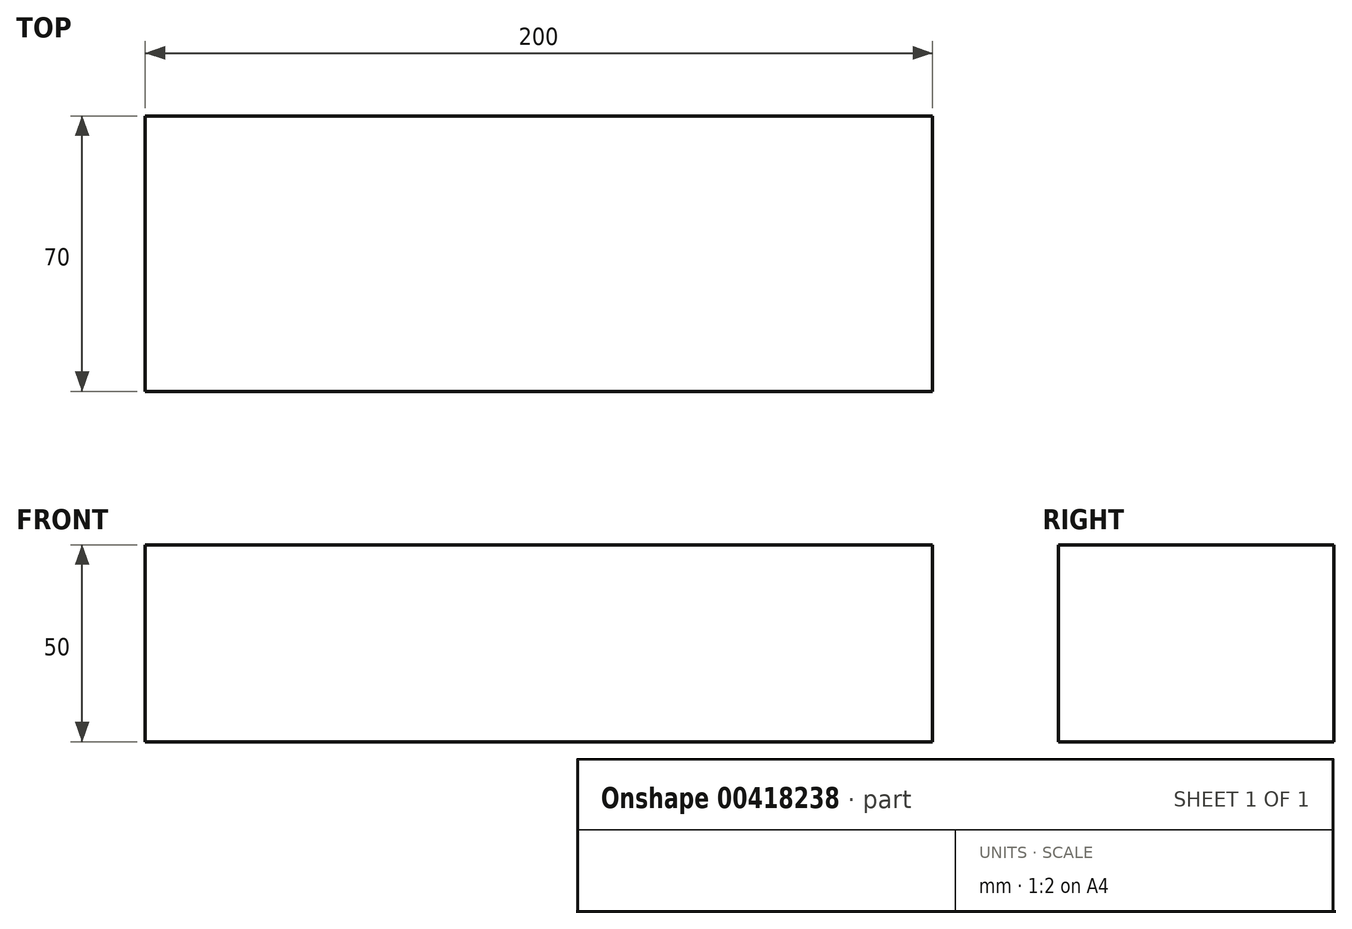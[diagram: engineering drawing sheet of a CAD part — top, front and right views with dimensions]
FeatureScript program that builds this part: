
annotation { "Feature Type Name" : "Feature", "Feature Type Description" : "" }
export const myFeature = defineFeature(function(context is Context, id is Id, definition is map)
    precondition{}
    {
        {
            var Q0;
            Q0=qCreatedBy(makeId("Top.planeOp"),FACE);
            var sketch = newSketch(context, id + "F0", { "sketchPlane" : qUnion([Q0])});
            skLineSegment(sketch, "E0.bottom", {"start": v(-97.6, 25.08) * mm, "end": v(102.4, 25.08) * mm});
            skLineSegment(sketch, "E0.top", {"start": v(-97.6, -44.92) * mm, "end": v(102.4, -44.92) * mm});
            skLineSegment(sketch, "E0.left", {"start": v(-97.6, 25.08) * mm, "end": v(-97.6, -44.92) * mm});
            skLineSegment(sketch, "E0.right", {"start": v(102.4, 25.08) * mm, "end": v(102.4, -44.92) * mm});
            skSolve(sketch);
        }
        {
            var Q0;
            Q0=makeQuery(id+"F0.imprint","IMPRINT",FACE,{"disambiguationData":[TD([[makeQuery(id+"F0.imprint","IMPRINT",EDGE,{"derivedFrom":sQuery(id+"F0.wireOp",EDGE,"E0.bottom")}),-1.0]])]});
            extrude(context, id + "F1", {"entities" : qUnion([Q0]), "depth" : 50 * mm});
        }
    });
